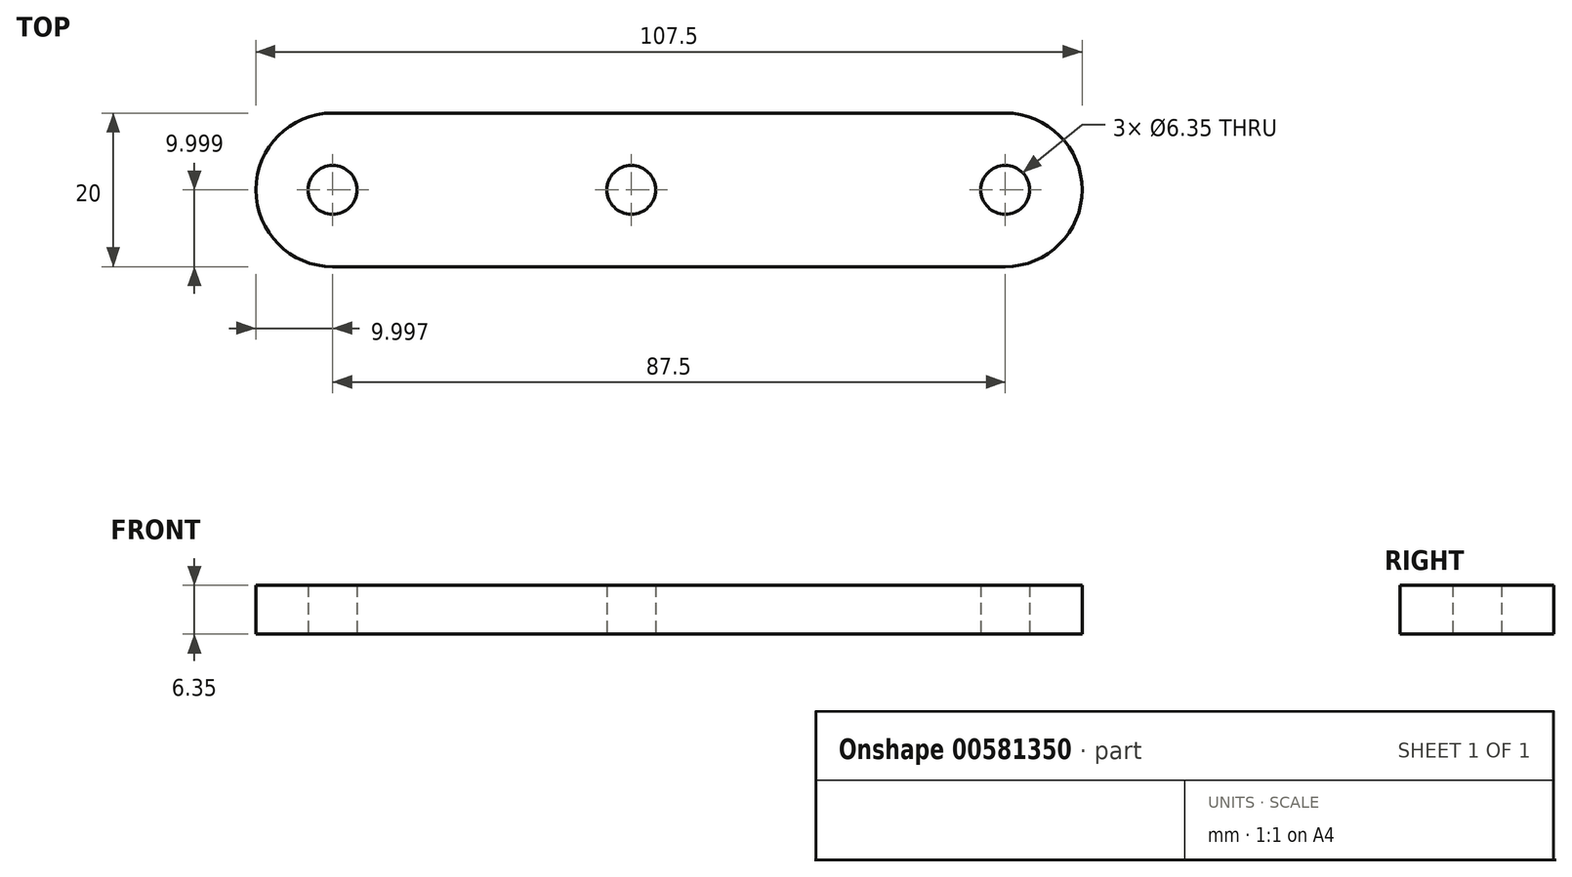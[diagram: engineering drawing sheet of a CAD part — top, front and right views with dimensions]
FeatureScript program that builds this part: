
annotation { "Feature Type Name" : "Feature", "Feature Type Description" : "" }
export const myFeature = defineFeature(function(context is Context, id is Id, definition is map)
    precondition{}
    {
        {
            var Q0;
            Q0=qCreatedBy(makeId("Top.planeOp"),FACE);
            var sketch = newSketch(context, id + "F0", { "sketchPlane" : qUnion([Q0])});
            skLineSegment(sketch, "E0", {"start": v(-37.1, 40.62) * mm, "end": v(50.4, 40.62) * mm});
            skLineSegment(sketch, "E1", {"start": v(-37.1, 60.62) * mm, "end": v(50.4, 60.62) * mm});
            skArc(sketch, "E2", {"start": v(-37.1, 60.62) * mm, "mid": v(-47.1, 50.62) * mm, "end": v(-37.1, 40.62) * mm});
            skArc(sketch, "E3", {"start": v(50.4, 40.62) * mm, "mid": v(60.4, 50.62) * mm, "end": v(50.4, 60.62) * mm});
            skSolve(sketch);
        }
        {
            var Q0;
            Q0=makeQuery(id+"F0.imprint","IMPRINT",FACE,{"disambiguationData":[TD([[makeQuery(id+"F0.imprint","IMPRINT",EDGE,{"derivedFrom":sQuery(id+"F0.wireOp",EDGE,"E0")}),1.0]])]});
            var sketch = newSketch(context, id + "F1", { "sketchPlane" : qUnion([Q0])});
            skCircle(sketch, "E4", {"center": v(-37.1, 50.62) * mm, "radius": 3.18 * mm});
            skCircle(sketch, "E5", {"center": v(50.4, 50.62) * mm, "radius": 3.18 * mm});
            skCircle(sketch, "E6", {"center": v(1.76, 50.62) * mm, "radius": 3.18 * mm});
            skSolve(sketch);
        }
        {
            var Q0;
            Q0 = qSketchRegion(id + "F0", true);
            extrude(context, id + "F2", {"entities" : qUnion([Q0]), "depth" : 6.35 * mm, "offsetDistance" : 25 * mm});
        }
        {
            var Q0;
            Q0 = qSketchRegion(id + "F1", true);
            extrude(context, id + "F3", {"entities" : qUnion([Q0]), "operationType" : NewBodyOperationType.REMOVE, "endBound" : BoundingType.THROUGH_ALL, "depth" : 25 * mm, "offsetDistance" : 25 * mm});
        }
    });
